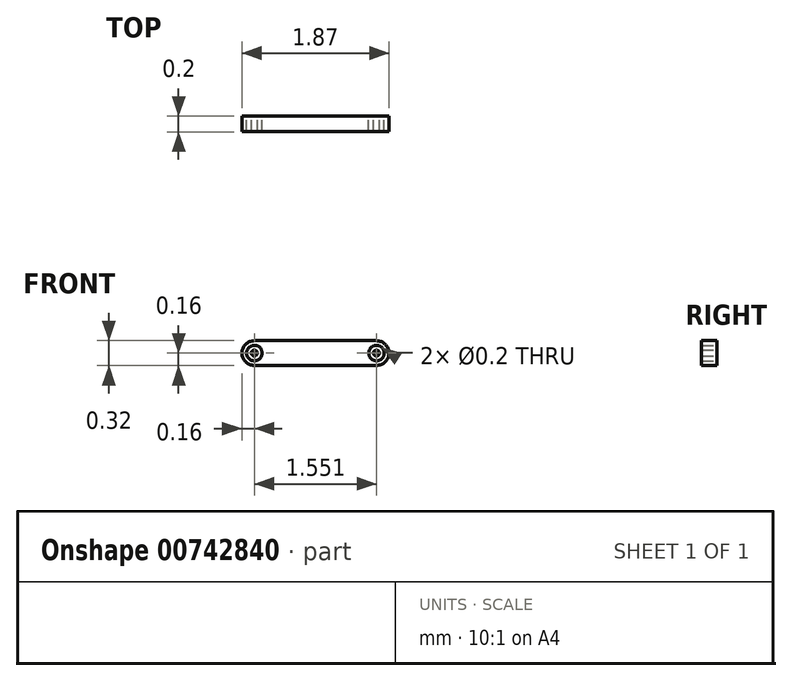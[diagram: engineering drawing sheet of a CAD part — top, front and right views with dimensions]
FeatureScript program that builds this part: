
annotation { "Feature Type Name" : "Feature", "Feature Type Description" : "" }
export const myFeature = defineFeature(function(context is Context, id is Id, definition is map)
    precondition{}
    {
        {
            var Q0;
            Q0=qCreatedBy(makeId("Front.planeOp"),FACE);
            var sketch = newSketch(context, id + "F0", { "sketchPlane" : qUnion([Q0])});
            skCircle(sketch, "E0", {"center": v(0, 0) * mm, "radius": 0.16 * mm});
            skCircle(sketch, "E1", {"center": v(1.55, 0) * mm, "radius": 0.16 * mm});
            skLineSegment(sketch, "E2", {"start": v(0, 0.16) * mm, "end": v(1.55, 0.16) * mm});
            skLineSegment(sketch, "E3", {"start": v(0, -0.16) * mm, "end": v(1.55, -0.16) * mm});
            skCircle(sketch, "E4", {"center": v(0, 0) * mm, "radius": 0.1 * mm});
            skCircle(sketch, "E5", {"center": v(1.55, 0) * mm, "radius": 0.1 * mm});
            skCircle(sketch, "E6", {"center": v(0, 0) * mm, "radius": 0.04 * mm});
            skCircle(sketch, "E7", {"center": v(1.55, 0) * mm, "radius": 0.04 * mm});
            skSolve(sketch);
        }
        {
            var Q0;
            Q0 = qSketchRegion(id + "F0", true);
            var Q1;
            Q1=makeQuery(id+"F0.imprint","IMPRINT",FACE,{"disambiguationData":[TD([[makeQuery(id+"F0.imprint","IMPRINT",EDGE,{"derivedFrom":sQuery(id+"F0.wireOp",EDGE,"E6")}),1.0]])]});
            var Q2;
            Q2=makeQuery(id+"F0.imprint","IMPRINT",FACE,{"disambiguationData":[TD([[makeQuery(id+"F0.imprint","IMPRINT",EDGE,{"derivedFrom":sQuery(id+"F0.wireOp",EDGE,"E7")}),1.0]])]});
            extrude(context, id + "F1", {"entities" : qUnion([Q0, Q1, Q2]), "depth" : 0.2 * mm, "offsetDistance" : 25 * mm});
        }
    });
